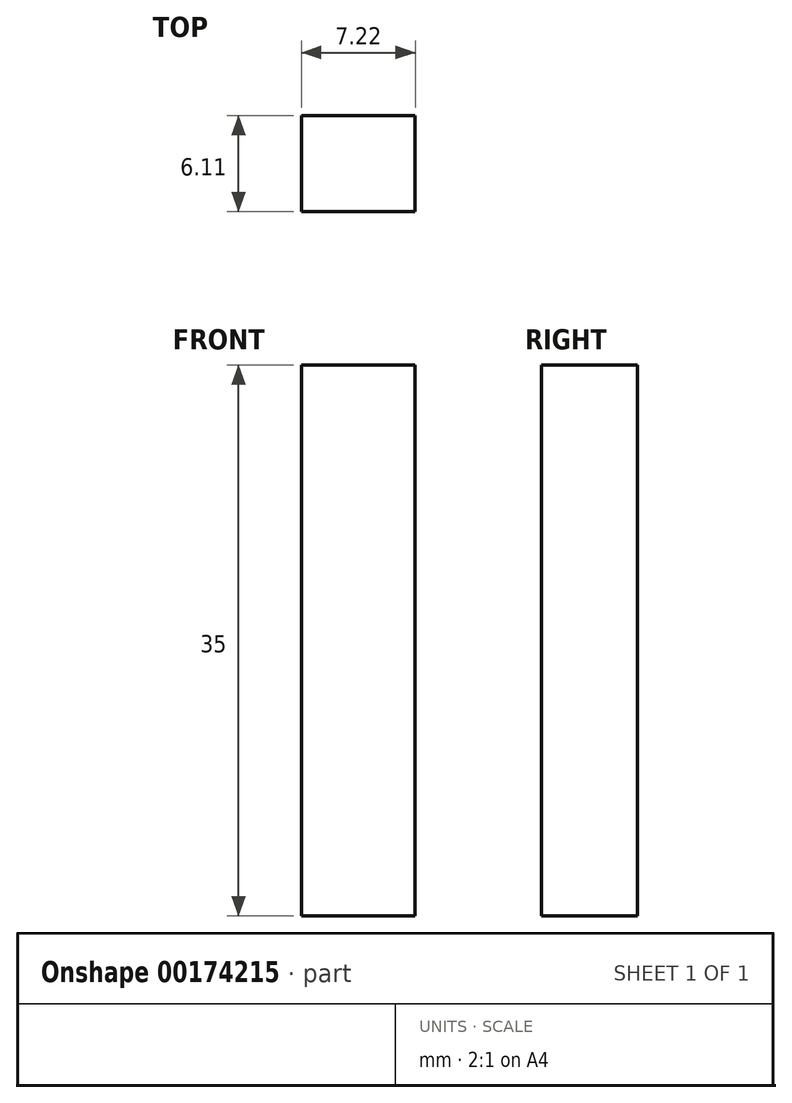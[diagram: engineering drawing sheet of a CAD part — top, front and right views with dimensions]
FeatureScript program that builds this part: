
annotation { "Feature Type Name" : "Feature", "Feature Type Description" : "" }
export const myFeature = defineFeature(function(context is Context, id is Id, definition is map)
    precondition{}
    {
        {
            var Q0;
            Q0=qCreatedBy(makeId("Top.planeOp"),FACE);
            var sketch = newSketch(context, id + "F0", { "sketchPlane" : qUnion([Q0])});
            skLineSegment(sketch, "E0.bottom", {"start": v(-49.2, 39.13) * mm, "end": v(-42, 39.13) * mm});
            skLineSegment(sketch, "E0.top", {"start": v(-49.2, 33.02) * mm, "end": v(-42, 33.02) * mm});
            skLineSegment(sketch, "E0.left", {"start": v(-49.2, 39.13) * mm, "end": v(-49.2, 33.02) * mm});
            skLineSegment(sketch, "E0.right", {"start": v(-42, 39.13) * mm, "end": v(-42, 33.02) * mm});
            skLineSegment(sketch, "E1.bottom", {"start": v(-3.6, 3.05) * mm, "end": v(3.6, 3.05) * mm});
            skLineSegment(sketch, "E1.top", {"start": v(-3.6, -3.05) * mm, "end": v(3.6, -3.05) * mm});
            skLineSegment(sketch, "E1.left", {"start": v(-3.6, 3.05) * mm, "end": v(-3.6, -3.05) * mm});
            skLineSegment(sketch, "E1.right", {"start": v(3.6, 3.05) * mm, "end": v(3.6, -3.05) * mm});
            skLineSegment(sketch, "E2.bottom", {"start": v(-26.4, 21.09) * mm, "end": v(-19.2, 21.09) * mm});
            skLineSegment(sketch, "E2.top", {"start": v(-26.4, 14.98) * mm, "end": v(-19.2, 14.98) * mm});
            skLineSegment(sketch, "E2.left", {"start": v(-26.4, 21.09) * mm, "end": v(-26.4, 14.98) * mm});
            skLineSegment(sketch, "E2.right", {"start": v(-19.2, 21.09) * mm, "end": v(-19.2, 14.98) * mm});
            skLineSegment(sketch, "E3.bottom", {"start": v(19.2, -14.98) * mm, "end": v(26.4, -14.98) * mm});
            skLineSegment(sketch, "E3.top", {"start": v(19.2, -21.09) * mm, "end": v(26.4, -21.09) * mm});
            skLineSegment(sketch, "E3.left", {"start": v(19.2, -14.98) * mm, "end": v(19.2, -21.09) * mm});
            skLineSegment(sketch, "E3.right", {"start": v(26.4, -14.98) * mm, "end": v(26.4, -21.09) * mm});
            skSolve(sketch);
        }
        {
            var Q0;
            Q0=makeQuery(id+"F0.imprint","IMPRINT",FACE,{"disambiguationData":[TD([[makeQuery(id+"F0.imprint","IMPRINT",EDGE,{"derivedFrom":sQuery(id+"F0.wireOp",EDGE,"E0.bottom")}),-1.0]])]});
            extrude(context, id + "F1", {"entities" : qUnion([Q0]), "depth" : 35 * mm});
        }
    });
